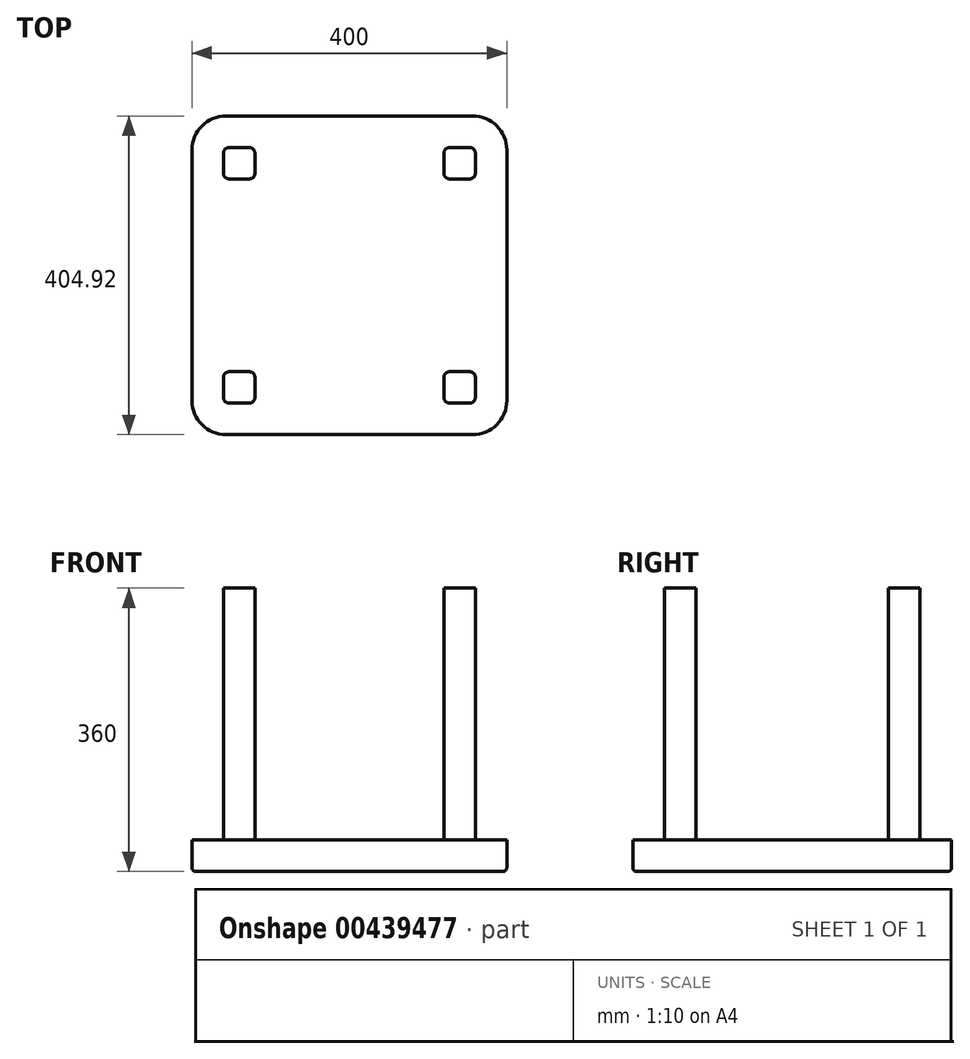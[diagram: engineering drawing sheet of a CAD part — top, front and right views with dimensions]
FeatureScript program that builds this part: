
annotation { "Feature Type Name" : "Feature", "Feature Type Description" : "" }
export const myFeature = defineFeature(function(context is Context, id is Id, definition is map)
    precondition{}
    {
        {
            var Q0;
            Q0=qCreatedBy(makeId("Top.planeOp"),FACE);
            var sketch = newSketch(context, id + "F0", { "sketchPlane" : qUnion([Q0])});
            skLineSegment(sketch, "E0.bottom", {"start": v(-134.46, 202.46) * mm, "end": v(265.54, 202.46) * mm});
            skLineSegment(sketch, "E0.top", {"start": v(-134.46, -202.46) * mm, "end": v(265.54, -202.46) * mm});
            skLineSegment(sketch, "E0.left", {"start": v(-134.46, 202.46) * mm, "end": v(-134.46, -202.46) * mm});
            skLineSegment(sketch, "E0.right", {"start": v(265.54, 202.46) * mm, "end": v(265.54, -202.46) * mm});
            skSolve(sketch);
        }
        {
            var Q0;
            Q0=makeQuery(id+"F0.imprint","IMPRINT",FACE,{"disambiguationData":[TD([[makeQuery(id+"F0.imprint","IMPRINT",EDGE,{"derivedFrom":sQuery(id+"F0.wireOp",EDGE,"E0.bottom")}),-1.0]])]});
            extrude(context, id + "F1", {"entities" : qUnion([Q0]), "depth" : 40 * mm});
        }
        {
            var Q0;
            Q0=makeQuery(id+"F1.opExtrude","SWEPT_EDGE",EDGE,{"disambiguationData":[OSD([sQuery(id+"F0.wireOp",EDGE,"E0.top"),sQuery(id+"F0.wireOp",EDGE,"E0.left")])]});
            var Q1;
            Q1=makeQuery(id+"F1.opExtrude","SWEPT_EDGE",EDGE,{"disambiguationData":[OSD([sQuery(id+"F0.wireOp",EDGE,"E0.bottom"),sQuery(id+"F0.wireOp",EDGE,"E0.left")])]});
            var Q2;
            Q2=makeQuery(id+"F1.opExtrude","SWEPT_EDGE",EDGE,{"disambiguationData":[OSD([sQuery(id+"F0.wireOp",EDGE,"E0.bottom"),sQuery(id+"F0.wireOp",EDGE,"E0.right")])]});
            var Q3;
            Q3=makeQuery(id+"F1.opExtrude","SWEPT_EDGE",EDGE,{"disambiguationData":[OSD([sQuery(id+"F0.wireOp",EDGE,"E0.top"),sQuery(id+"F0.wireOp",EDGE,"E0.right")])]});
            fillet(context, id + "F2", {"entities" : qUnion([Q0, Q1, Q2, Q3]), "radius" : 43.46 * mm, "tangentPropagation" : true, "allowEdgeOverflow" : false});
        }
        {
            var Q0;
            Q0=qCreatedBy(makeId("Top.planeOp"),FACE);
            var sketch = newSketch(context, id + "F3", { "sketchPlane" : qUnion([Q0])});
            skLineSegment(sketch, "E1.bottom", {"start": v(-94.46, -162.46) * mm, "end": v(-54.46, -162.46) * mm});
            skLineSegment(sketch, "E1.top", {"start": v(-94.46, -122.46) * mm, "end": v(-54.46, -122.46) * mm});
            skLineSegment(sketch, "E1.left", {"start": v(-94.46, -162.46) * mm, "end": v(-94.46, -122.46) * mm});
            skLineSegment(sketch, "E1.right", {"start": v(-54.46, -162.46) * mm, "end": v(-54.46, -122.46) * mm});
            skSolve(sketch);
        }
        {
            var Q0;
            Q0=makeQuery(id+"F3.imprint","IMPRINT",FACE,{"disambiguationData":[TD([[makeQuery(id+"F3.imprint","IMPRINT",EDGE,{"derivedFrom":sQuery(id+"F3.wireOp",EDGE,"E1.bottom")}),1.0]])]});
            extrude(context, id + "F4", {"entities" : qUnion([Q0]), "operationType" : NewBodyOperationType.ADD, "depth" : 360 * mm});
        }
        {
            var Q0;
            Q0=makeQuery(id+"F4.opExtrude","SWEPT_EDGE",EDGE,{"disambiguationData":[OSD([sQuery(id+"F3.wireOp",EDGE,"E1.bottom"),sQuery(id+"F3.wireOp",EDGE,"E1.right")])]});
            var Q1;
            Q1=makeQuery(id+"F4.opExtrude","SWEPT_EDGE",EDGE,{"disambiguationData":[OSD([sQuery(id+"F3.wireOp",EDGE,"E1.top"),sQuery(id+"F3.wireOp",EDGE,"E1.right")])]});
            var Q2;
            Q2=makeQuery(id+"F4.opExtrude","SWEPT_EDGE",EDGE,{"disambiguationData":[OSD([sQuery(id+"F3.wireOp",EDGE,"E1.top"),sQuery(id+"F3.wireOp",EDGE,"E1.left")])]});
            var Q3;
            Q3=makeQuery(id+"F4.opExtrude","SWEPT_EDGE",EDGE,{"disambiguationData":[OSD([sQuery(id+"F3.wireOp",EDGE,"E1.bottom"),sQuery(id+"F3.wireOp",EDGE,"E1.left")])]});
            fillet(context, id + "F5", {"entities" : qUnion([Q0, Q1, Q2, Q3]), "radius" : 7.24 * mm, "tangentPropagation" : true, "allowEdgeOverflow" : false});
        }
        {
            var Q0;
            Q0=qCreatedBy(makeId("Top.planeOp"),FACE);
            var sketch = newSketch(context, id + "F6", { "sketchPlane" : qUnion([Q0])});
            skLineSegment(sketch, "E2.bottom", {"start": v(-94.46, 162.46) * mm, "end": v(-54.46, 162.46) * mm});
            skLineSegment(sketch, "E2.top", {"start": v(-94.46, 122.46) * mm, "end": v(-54.46, 122.46) * mm});
            skLineSegment(sketch, "E2.left", {"start": v(-94.46, 162.46) * mm, "end": v(-94.46, 122.46) * mm});
            skLineSegment(sketch, "E2.right", {"start": v(-54.46, 162.46) * mm, "end": v(-54.46, 122.46) * mm});
            skLineSegment(sketch, "E3.bottom", {"start": v(185.54, 162.46) * mm, "end": v(225.54, 162.46) * mm});
            skLineSegment(sketch, "E3.top", {"start": v(185.54, 122.46) * mm, "end": v(225.54, 122.46) * mm});
            skLineSegment(sketch, "E3.left", {"start": v(185.54, 162.46) * mm, "end": v(185.54, 122.46) * mm});
            skLineSegment(sketch, "E3.right", {"start": v(225.54, 162.46) * mm, "end": v(225.54, 122.46) * mm});
            skLineSegment(sketch, "E4.bottom", {"start": v(185.54, -122.46) * mm, "end": v(225.54, -122.46) * mm});
            skLineSegment(sketch, "E4.top", {"start": v(185.54, -162.46) * mm, "end": v(225.54, -162.46) * mm});
            skLineSegment(sketch, "E4.left", {"start": v(185.54, -122.46) * mm, "end": v(185.54, -162.46) * mm});
            skLineSegment(sketch, "E4.right", {"start": v(225.54, -122.46) * mm, "end": v(225.54, -162.46) * mm});
            skSolve(sketch);
        }
        {
            var Q0;
            Q0=makeQuery(id+"F6.imprint","IMPRINT",FACE,{"disambiguationData":[TD([[makeQuery(id+"F6.imprint","IMPRINT",EDGE,{"derivedFrom":sQuery(id+"F6.wireOp",EDGE,"E4.bottom")}),-1.0]])]});
            var Q1;
            Q1=makeQuery(id+"F6.imprint","IMPRINT",FACE,{"disambiguationData":[TD([[makeQuery(id+"F6.imprint","IMPRINT",EDGE,{"derivedFrom":sQuery(id+"F6.wireOp",EDGE,"E3.bottom")}),-1.0]])]});
            var Q2;
            Q2=makeQuery(id+"F6.imprint","IMPRINT",FACE,{"disambiguationData":[TD([[makeQuery(id+"F6.imprint","IMPRINT",EDGE,{"derivedFrom":sQuery(id+"F6.wireOp",EDGE,"E2.bottom")}),-1.0]])]});
            extrude(context, id + "F7", {"entities" : qUnion([Q0, Q1, Q2]), "operationType" : NewBodyOperationType.ADD, "depth" : 360 * mm});
        }
        {
            var Q0;
            Q0=makeQuery(id+"F7.opExtrude","SWEPT_EDGE",EDGE,{"disambiguationData":[OSD([sQuery(id+"F6.wireOp",EDGE,"E2.bottom"),sQuery(id+"F6.wireOp",EDGE,"E2.right")])]});
            var Q1;
            Q1=makeQuery(id+"F7.opExtrude","SWEPT_EDGE",EDGE,{"disambiguationData":[OSD([sQuery(id+"F6.wireOp",EDGE,"E2.bottom"),sQuery(id+"F6.wireOp",EDGE,"E2.left")])]});
            var Q2;
            Q2=makeQuery(id+"F7.opExtrude","SWEPT_EDGE",EDGE,{"disambiguationData":[OSD([sQuery(id+"F6.wireOp",EDGE,"E2.top"),sQuery(id+"F6.wireOp",EDGE,"E2.left")])]});
            var Q3;
            Q3=makeQuery(id+"F7.opExtrude","SWEPT_EDGE",EDGE,{"disambiguationData":[OSD([sQuery(id+"F6.wireOp",EDGE,"E2.top"),sQuery(id+"F6.wireOp",EDGE,"E2.right")])]});
            var Q4;
            Q4=makeQuery(id+"F7.opExtrude","SWEPT_EDGE",EDGE,{"disambiguationData":[OSD([sQuery(id+"F6.wireOp",EDGE,"E3.top"),sQuery(id+"F6.wireOp",EDGE,"E3.right")])]});
            var Q5;
            Q5=makeQuery(id+"F7.opExtrude","SWEPT_EDGE",EDGE,{"disambiguationData":[OSD([sQuery(id+"F6.wireOp",EDGE,"E3.bottom"),sQuery(id+"F6.wireOp",EDGE,"E3.right")])]});
            var Q6;
            Q6=makeQuery(id+"F7.opExtrude","SWEPT_EDGE",EDGE,{"disambiguationData":[OSD([sQuery(id+"F6.wireOp",EDGE,"E3.top"),sQuery(id+"F6.wireOp",EDGE,"E3.left")])]});
            var Q7;
            Q7=makeQuery(id+"F7.opExtrude","SWEPT_EDGE",EDGE,{"disambiguationData":[OSD([sQuery(id+"F6.wireOp",EDGE,"E3.bottom"),sQuery(id+"F6.wireOp",EDGE,"E3.left")])]});
            var Q8;
            Q8=makeQuery(id+"F7.opExtrude","SWEPT_EDGE",EDGE,{"disambiguationData":[OSD([sQuery(id+"F6.wireOp",EDGE,"E4.top"),sQuery(id+"F6.wireOp",EDGE,"E4.right")])]});
            var Q9;
            Q9=makeQuery(id+"F7.opExtrude","SWEPT_EDGE",EDGE,{"disambiguationData":[OSD([sQuery(id+"F6.wireOp",EDGE,"E4.bottom"),sQuery(id+"F6.wireOp",EDGE,"E4.right")])]});
            var Q10;
            Q10=makeQuery(id+"F7.opExtrude","SWEPT_EDGE",EDGE,{"disambiguationData":[OSD([sQuery(id+"F6.wireOp",EDGE,"E4.top"),sQuery(id+"F6.wireOp",EDGE,"E4.left")])]});
            var Q11;
            Q11=makeQuery(id+"F7.opExtrude","SWEPT_EDGE",EDGE,{"disambiguationData":[OSD([sQuery(id+"F6.wireOp",EDGE,"E4.bottom"),sQuery(id+"F6.wireOp",EDGE,"E4.left")])]});
            fillet(context, id + "F8", {"entities" : qUnion([Q0, Q1, Q2, Q3, Q4, Q5, Q6, Q7, Q8, Q9, Q10, Q11]), "radius" : 7.24 * mm, "tangentPropagation" : true, "allowEdgeOverflow" : false});
        }
        {
            var Q0;
            Q0=makeQuery(id+"F1.opExtrude","CAP_EDGE",EDGE,{"disambiguationData":[OSD([sQuery(id+"F0.wireOp",EDGE,"E0.right")])],"isStart":true});
            var Q1;
            {var subQ0=sQuery(id+"F0.wireOp",EDGE,"E0.right");var subQ1=sQuery(id+"F0.wireOp",EDGE,"E0.bottom");Q1=makeQuery(id+"F2.opFillet","BLEND_EDGE",EDGE,{"blendedFrom":[makeQuery(id+"F1.opExtrude","SWEPT_EDGE",EDGE,{"disambiguationData":[OSD([subQ1,subQ0])]}),makeQuery(id+"F1.opExtrude","CAP_FACE",FACE,{"disambiguationData":[OSD([subQ1,sQuery(id+"F0.wireOp",EDGE,"E0.top"),sQuery(id+"F0.wireOp",EDGE,"E0.left"),subQ0])],"isStart":true})],"blendedInto":[makeQuery(id+"F1.opExtrude","CAP_FACE",FACE,{"disambiguationData":[OSD([subQ1,sQuery(id+"F0.wireOp",EDGE,"E0.top"),sQuery(id+"F0.wireOp",EDGE,"E0.left"),subQ0])],"isStart":true})]});}
            var Q2;
            Q2=makeQuery(id+"F1.opExtrude","CAP_FACE",FACE,{"disambiguationData":[OSD([sQuery(id+"F0.wireOp",EDGE,"E0.bottom"),sQuery(id+"F0.wireOp",EDGE,"E0.top"),sQuery(id+"F0.wireOp",EDGE,"E0.left"),sQuery(id+"F0.wireOp",EDGE,"E0.right")])],"isStart":true});
            fillet(context, id + "F9", {"entities" : qUnion([Q0, Q1, Q2]), "radius" : 5 * mm, "tangentPropagation" : true, "allowEdgeOverflow" : false});
        }
    });
